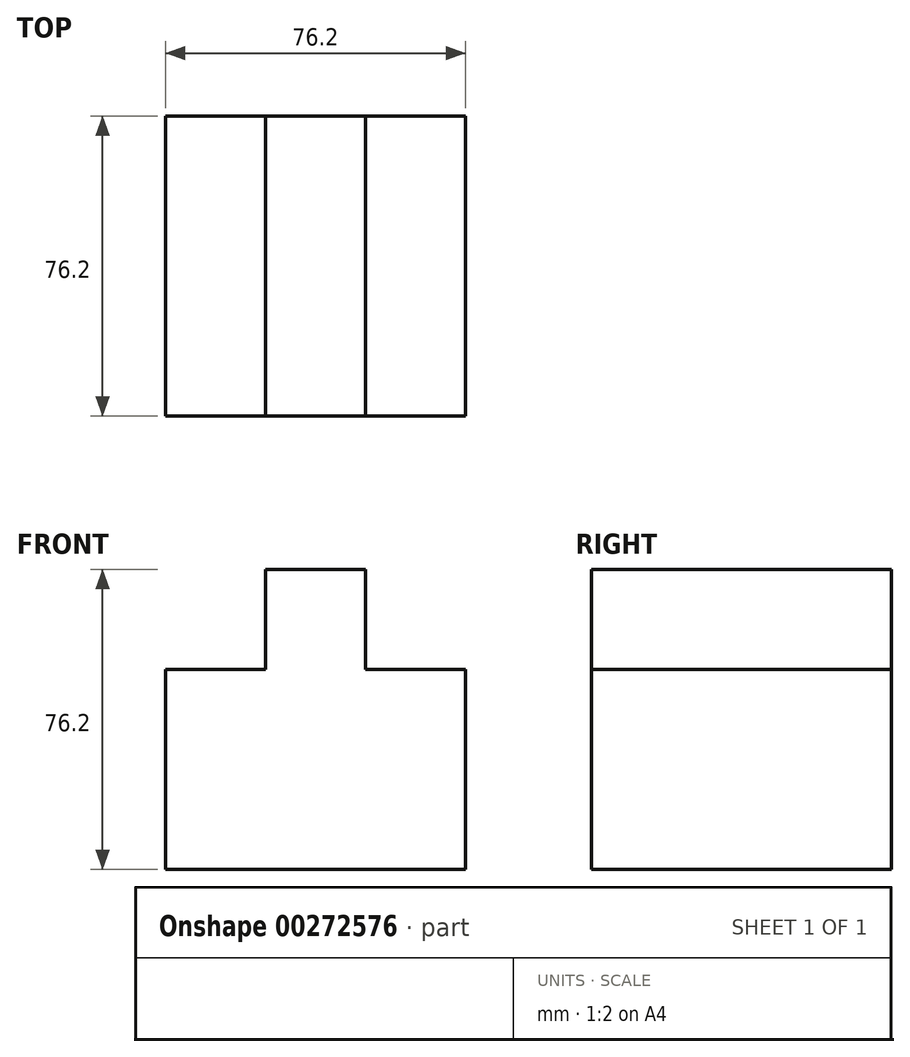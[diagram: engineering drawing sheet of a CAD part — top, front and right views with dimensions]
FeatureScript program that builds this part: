
annotation { "Feature Type Name" : "Feature", "Feature Type Description" : "" }
export const myFeature = defineFeature(function(context is Context, id is Id, definition is map)
    precondition{}
    {
        {
            var Q0;
            Q0=qCreatedBy(makeId("Front.planeOp"),FACE);
            var sketch = newSketch(context, id + "F0", { "sketchPlane" : qUnion([Q0])});
            skLineSegment(sketch, "E0", {"start": v(0, 0) * mm, "end": v(-76.2, 0) * mm});
            skLineSegment(sketch, "E1", {"start": v(-76.2, 0) * mm, "end": v(-76.2, 50.8) * mm});
            skLineSegment(sketch, "E2", {"start": v(-76.2, 50.8) * mm, "end": v(-50.8, 50.8) * mm});
            skLineSegment(sketch, "E3", {"start": v(-50.8, 50.8) * mm, "end": v(-50.8, 76.2) * mm});
            skLineSegment(sketch, "E4", {"start": v(-50.8, 76.2) * mm, "end": v(-25.4, 76.2) * mm});
            skLineSegment(sketch, "E5", {"start": v(-25.4, 76.2) * mm, "end": v(-25.4, 50.8) * mm});
            skLineSegment(sketch, "E6", {"start": v(-25.4, 50.8) * mm, "end": v(0, 50.8) * mm});
            skLineSegment(sketch, "E7", {"start": v(0, 50.8) * mm, "end": v(0, 0) * mm});
            skSolve(sketch);
        }
        {
            var Q0;
            Q0 = qSketchRegion(id + "F0", true);
            extrude(context, id + "F1", {"entities" : qUnion([Q0]), "depth" : 76.2 * mm});
        }
    });
